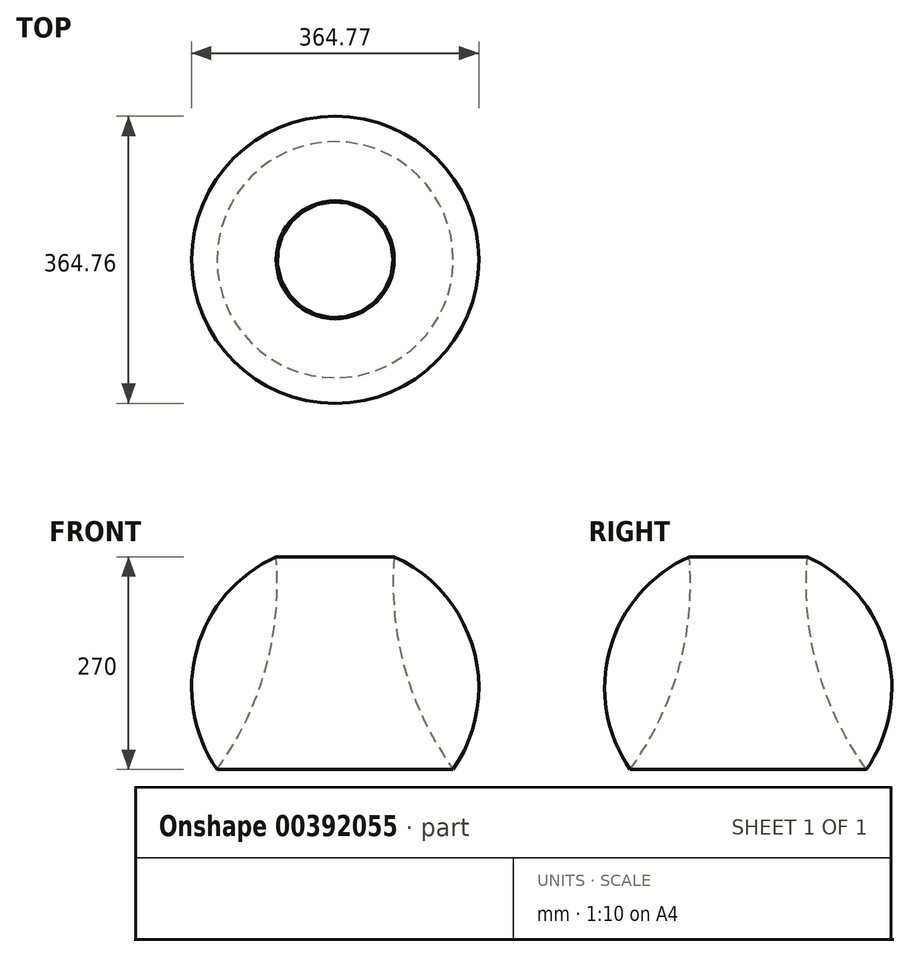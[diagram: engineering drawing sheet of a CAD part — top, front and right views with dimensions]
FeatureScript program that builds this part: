
annotation { "Feature Type Name" : "Feature", "Feature Type Description" : "" }
export const myFeature = defineFeature(function(context is Context, id is Id, definition is map)
    precondition{}
    {
        {
            var Q0;
            Q0=qCreatedBy(makeId("Front.planeOp"),FACE);
            var sketch = newSketch(context, id + "F0", { "sketchPlane" : qUnion([Q0])});
            skArc(sketch, "E0", {"start": v(-112.04, -222.88) * mm, "mid": v(-86.3, -70.32) * mm, "end": v(-187.04, 47.12) * mm});
            skLineSegment(sketch, "E1", {"start": v(-262.04, 63.25) * mm, "end": v(-262.04, -301.52) * mm, "construction": true});
            skLineSegment(sketch, "E2", {"start": v(-262.04, 47.12) * mm, "end": v(-187.04, 47.12) * mm, "construction": true});
            skLineSegment(sketch, "E3", {"start": v(-262.04, -222.88) * mm, "end": v(-112.04, -222.88) * mm, "construction": true});
            skLineSegment(sketch, "E4", {"start": v(-262.04, -52.88) * mm, "end": v(-183.05, -52.88) * mm, "construction": true});
            skArc(sketch, "E5", {"start": v(-187.04, 47.12) * mm, "mid": v(-173.82, -94.63) * mm, "end": v(-112.04, -222.88) * mm});
            skPoint(sketch, "E5.third.point", {"position": v(600.82, 121.56) * mm});
            skSolve(sketch);
        }
        {
            var Q0;
            Q0 = qSketchRegion(id + "F0", true);
            var Q1;
            Q1=sQuery(id+"F0.wireOp",EDGE,"E1");
            revolve(context, id + "F1", {"entities" : qUnion([Q0]), "axis" : qUnion([Q1]), "revolveType" : RevolveType.FULL});
        }
    });
